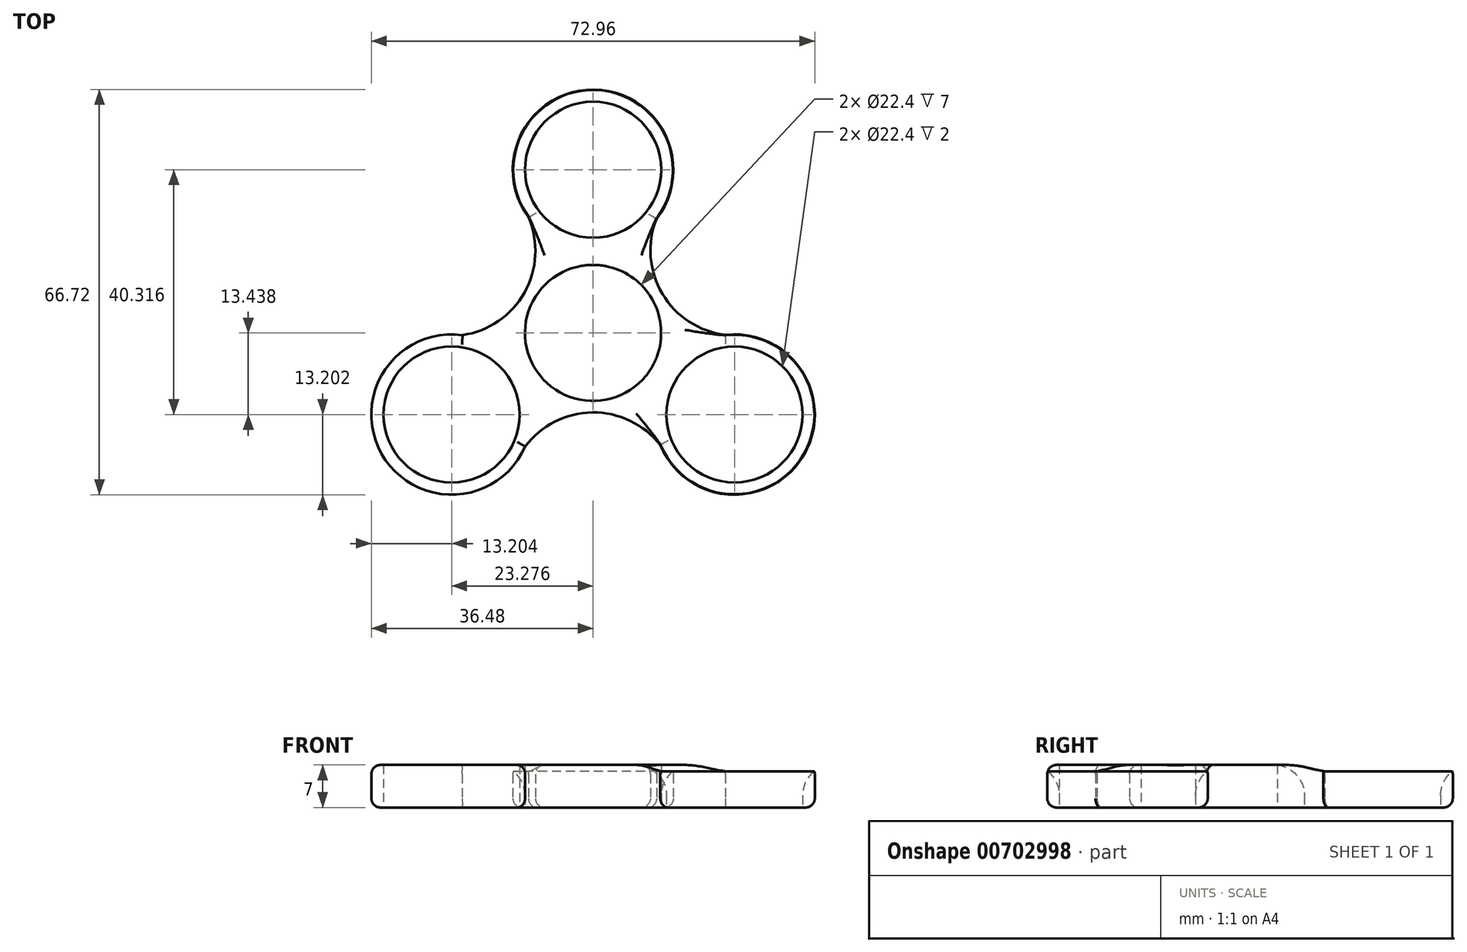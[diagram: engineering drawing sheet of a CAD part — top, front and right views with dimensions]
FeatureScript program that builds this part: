
annotation { "Feature Type Name" : "Feature", "Feature Type Description" : "" }
export const myFeature = defineFeature(function(context is Context, id is Id, definition is map)
    precondition{}
    {
        {
            var Q0;
            Q0=qCreatedBy(makeId("Top.planeOp"),FACE);
            var sketch = newSketch(context, id + "F0", { "sketchPlane" : qUnion([Q0])});
            skCircle(sketch, "E0", {"center": v(0, 0) * mm, "radius": 11.2 * mm});
            skCircle(sketch, "E1", {"center": v(0, 0) * mm, "radius": 13.2 * mm});
            skCircle(sketch, "E2", {"center": v(0, 26.88) * mm, "radius": 11.2 * mm});
            skArc(sketch, "E3", {"start": v(10.44, 18.8) * mm, "mid": v(0.14, 40.08) * mm, "end": v(-10.61, 19.03) * mm});
            skArc(sketch, "E4.1.0", {"start": v(-21.5, -0.36) * mm, "mid": v(-34.78, -19.92) * mm, "end": v(-11.17, -18.7) * mm});
            skCircle(sketch, "E4.1.1", {"center": v(-23.28, -13.44) * mm, "radius": 11.2 * mm});
            skArc(sketch, "E4.2.0", {"start": v(11.06, -18.44) * mm, "mid": v(34.64, -20.16) * mm, "end": v(21.78, -0.32) * mm});
            skCircle(sketch, "E4.2.1", {"center": v(23.28, -13.44) * mm, "radius": 11.2 * mm});
            skArc(sketch, "E5", {"start": v(10.44, 18.8) * mm, "mid": v(11.4, 6.44) * mm, "end": v(21.78, -0.32) * mm});
            skArc(sketch, "E6.1.0", {"start": v(-21.5, -0.36) * mm, "mid": v(-11.28, 6.65) * mm, "end": v(-10.61, 19.03) * mm});
            skArc(sketch, "E6.2.0", {"start": v(11.06, -18.44) * mm, "mid": v(-0.12, -13.1) * mm, "end": v(-11.17, -18.7) * mm});
            skSolve(sketch);
        }
        {
            var Q0;
            {var subQ1=sQuery(id+"F0.wireOp",EDGE,"E4.1.0");Q0=makeQuery(id+"F0.imprint","IMPRINT",FACE,{"disambiguationData":[TD([[makeQuery(id+"F0.imprint","IMPRINT",EDGE,{"derivedFrom":subQ1}),1.0]])]});}
            var Q1;
            Q1=makeQuery(id+"F0.imprint","IMPRINT",FACE,{"disambiguationData":[TD([[makeQuery(id+"F0.imprint","IMPRINT",EDGE,{"derivedFrom":sQuery(id+"F0.wireOp",EDGE,"E2")}),-1.0]])]});
            var Q2;
            Q2=makeQuery(id+"F0.imprint","IMPRINT",FACE,{"disambiguationData":[TD([[makeQuery(id+"F0.imprint","IMPRINT",EDGE,{"derivedFrom":sQuery(id+"F0.wireOp",EDGE,"E0")}),-1.0]])]});
            var Q3;
            {var subQ1=sQuery(id+"F0.wireOp",EDGE,"E4.2.0");Q3=makeQuery(id+"F0.imprint","IMPRINT",FACE,{"disambiguationData":[TD([[makeQuery(id+"F0.imprint","IMPRINT",EDGE,{"derivedFrom":subQ1}),1.0]])]});}
            extrude(context, id + "F1", {"entities" : qUnion([Q0, Q1, Q2, Q3]), "depth" : 7 * mm, "offsetDistance" : 25 * mm});
        }
        {
            var Q0;
            Q0=makeQuery(id+"F1.opExtrude","CAP_EDGE",EDGE,{"disambiguationData":[OSD([sQuery(id+"F0.wireOp",EDGE,"E4.1.0")])],"isStart":false});
            var Q1;
            Q1=makeQuery(id+"F1.opExtrude","CAP_EDGE",EDGE,{"disambiguationData":[OSD([sQuery(id+"F0.wireOp",EDGE,"E6.1.0")])],"isStart":false});
            var Q2;
            Q2=makeQuery(id+"F1.opExtrude","CAP_EDGE",EDGE,{"disambiguationData":[OSD([sQuery(id+"F0.wireOp",EDGE,"E6.2.0")])],"isStart":false});
            var Q3;
            Q3=makeQuery(id+"F1.opExtrude","CAP_EDGE",EDGE,{"disambiguationData":[OSD([sQuery(id+"F0.wireOp",EDGE,"E6.2.0")])],"isStart":true});
            var Q4;
            Q4=makeQuery(id+"F1.opExtrude","CAP_EDGE",EDGE,{"disambiguationData":[OSD([sQuery(id+"F0.wireOp",EDGE,"E3")])],"isStart":false});
            var Q5;
            Q5=makeQuery(id+"F1.opExtrude","CAP_EDGE",EDGE,{"disambiguationData":[OSD([sQuery(id+"F0.wireOp",EDGE,"E5")])],"isStart":false});
            var Q6;
            Q6=makeQuery(id+"F1.opExtrude","CAP_EDGE",EDGE,{"disambiguationData":[OSD([sQuery(id+"F0.wireOp",EDGE,"E4.2.0")])],"isStart":false});
            fillet(context, id + "F2", {"entities" : qUnion([Q0, Q1, Q2, Q3, Q4, Q5, Q6]), "radius" : 1.5 * mm, "tangentPropagation" : true, "allowEdgeOverflow" : false});
        }
        {
            var Q0;
            Q0=makeQuery(id+"F1.opExtrude","CAP_EDGE",EDGE,{"disambiguationData":[OSD([sQuery(id+"F0.wireOp",EDGE,"E4.1.0")])],"isStart":true});
            var Q1;
            Q1=makeQuery(id+"F1.opExtrude","CAP_EDGE",EDGE,{"disambiguationData":[OSD([sQuery(id+"F0.wireOp",EDGE,"E6.1.0")])],"isStart":true});
            var Q2;
            Q2=makeQuery(id+"F1.opExtrude","CAP_EDGE",EDGE,{"disambiguationData":[OSD([sQuery(id+"F0.wireOp",EDGE,"E3")])],"isStart":true});
            var Q3;
            Q3=makeQuery(id+"F1.opExtrude","CAP_EDGE",EDGE,{"disambiguationData":[OSD([sQuery(id+"F0.wireOp",EDGE,"E5")])],"isStart":true});
            var Q4;
            Q4=makeQuery(id+"F1.opExtrude","CAP_EDGE",EDGE,{"disambiguationData":[OSD([sQuery(id+"F0.wireOp",EDGE,"E4.2.0")])],"isStart":true});
            var Q5;
            {var subQ0=sQuery(id+"F0.wireOp",EDGE,"E6.2.0");Q5=makeQuery(id+"F2.opFillet","BLEND_EDGE",EDGE,{"blendedFrom":[makeQuery(id+"F1.opExtrude","CAP_EDGE",EDGE,{"disambiguationData":[OSD([subQ0])],"isStart":true}),makeQuery(id+"F1.opExtrude","CAP_FACE",FACE,{"disambiguationData":[OSD([sQuery(id+"F0.wireOp",EDGE,"E0"),sQuery(id+"F0.wireOp",EDGE,"E2"),sQuery(id+"F0.wireOp",EDGE,"E3"),sQuery(id+"F0.wireOp",EDGE,"E4.1.0"),sQuery(id+"F0.wireOp",EDGE,"E4.1.1"),sQuery(id+"F0.wireOp",EDGE,"E4.2.0"),sQuery(id+"F0.wireOp",EDGE,"E4.2.1"),sQuery(id+"F0.wireOp",EDGE,"E5"),sQuery(id+"F0.wireOp",EDGE,"E6.1.0"),subQ0])],"isStart":true})],"blendedInto":[makeQuery(id+"F1.opExtrude","CAP_FACE",FACE,{"disambiguationData":[OSD([sQuery(id+"F0.wireOp",EDGE,"E0"),sQuery(id+"F0.wireOp",EDGE,"E2"),sQuery(id+"F0.wireOp",EDGE,"E3"),sQuery(id+"F0.wireOp",EDGE,"E4.1.0"),sQuery(id+"F0.wireOp",EDGE,"E4.1.1"),sQuery(id+"F0.wireOp",EDGE,"E4.2.0"),sQuery(id+"F0.wireOp",EDGE,"E4.2.1"),sQuery(id+"F0.wireOp",EDGE,"E5"),sQuery(id+"F0.wireOp",EDGE,"E6.1.0"),subQ0])],"isStart":true})]});}
            fillet(context, id + "F3", {"entities" : qUnion([Q0, Q1, Q2, Q3, Q4, Q5]), "radius" : 1.5 * mm, "tangentPropagation" : true, "allowEdgeOverflow" : false});
        }
        {
            var Q0;
            {var subQ0=sQuery(id+"F0.wireOp",EDGE,"E6.2.0");Q0=makeQuery(id+"F2.opFillet","BLEND_EDGE",EDGE,{"blendedFrom":[makeQuery(id+"F1.opExtrude","CAP_EDGE",EDGE,{"disambiguationData":[OSD([subQ0])],"isStart":false}),makeQuery(id+"F1.opExtrude","CAP_FACE",FACE,{"disambiguationData":[OSD([sQuery(id+"F0.wireOp",EDGE,"E0"),sQuery(id+"F0.wireOp",EDGE,"E2"),sQuery(id+"F0.wireOp",EDGE,"E3"),sQuery(id+"F0.wireOp",EDGE,"E4.1.0"),sQuery(id+"F0.wireOp",EDGE,"E4.1.1"),sQuery(id+"F0.wireOp",EDGE,"E4.2.0"),sQuery(id+"F0.wireOp",EDGE,"E4.2.1"),sQuery(id+"F0.wireOp",EDGE,"E5"),sQuery(id+"F0.wireOp",EDGE,"E6.1.0"),subQ0])],"isStart":false})],"blendedInto":[makeQuery(id+"F1.opExtrude","CAP_FACE",FACE,{"disambiguationData":[OSD([sQuery(id+"F0.wireOp",EDGE,"E0"),sQuery(id+"F0.wireOp",EDGE,"E2"),sQuery(id+"F0.wireOp",EDGE,"E3"),sQuery(id+"F0.wireOp",EDGE,"E4.1.0"),sQuery(id+"F0.wireOp",EDGE,"E4.1.1"),sQuery(id+"F0.wireOp",EDGE,"E4.2.0"),sQuery(id+"F0.wireOp",EDGE,"E4.2.1"),sQuery(id+"F0.wireOp",EDGE,"E5"),sQuery(id+"F0.wireOp",EDGE,"E6.1.0"),subQ0])],"isStart":false})]});}
            var Q1;
            {var subQ0=sQuery(id+"F0.wireOp",EDGE,"E4.1.0");Q1=makeQuery(id+"F2.opFillet","BLEND_EDGE",EDGE,{"blendedFrom":[makeQuery(id+"F1.opExtrude","CAP_EDGE",EDGE,{"disambiguationData":[OSD([subQ0])],"isStart":false}),makeQuery(id+"F1.opExtrude","SWEPT_FACE",FACE,{"disambiguationData":[OSD([subQ0])]})],"blendedInto":[makeQuery(id+"F1.opExtrude","SWEPT_FACE",FACE,{"disambiguationData":[OSD([subQ0])]})]});}
            var Q2;
            {var subQ0=sQuery(id+"F0.wireOp",EDGE,"E6.1.0");Q2=makeQuery(id+"F2.opFillet","BLEND_EDGE",EDGE,{"blendedFrom":[makeQuery(id+"F1.opExtrude","CAP_EDGE",EDGE,{"disambiguationData":[OSD([subQ0])],"isStart":false}),makeQuery(id+"F1.opExtrude","CAP_FACE",FACE,{"disambiguationData":[OSD([sQuery(id+"F0.wireOp",EDGE,"E0"),sQuery(id+"F0.wireOp",EDGE,"E2"),sQuery(id+"F0.wireOp",EDGE,"E3"),sQuery(id+"F0.wireOp",EDGE,"E4.1.0"),sQuery(id+"F0.wireOp",EDGE,"E4.1.1"),sQuery(id+"F0.wireOp",EDGE,"E4.2.0"),sQuery(id+"F0.wireOp",EDGE,"E4.2.1"),sQuery(id+"F0.wireOp",EDGE,"E5"),subQ0,sQuery(id+"F0.wireOp",EDGE,"E6.2.0")])],"isStart":false})],"blendedInto":[makeQuery(id+"F1.opExtrude","CAP_FACE",FACE,{"disambiguationData":[OSD([sQuery(id+"F0.wireOp",EDGE,"E0"),sQuery(id+"F0.wireOp",EDGE,"E2"),sQuery(id+"F0.wireOp",EDGE,"E3"),sQuery(id+"F0.wireOp",EDGE,"E4.1.0"),sQuery(id+"F0.wireOp",EDGE,"E4.1.1"),sQuery(id+"F0.wireOp",EDGE,"E4.2.0"),sQuery(id+"F0.wireOp",EDGE,"E4.2.1"),sQuery(id+"F0.wireOp",EDGE,"E5"),subQ0,sQuery(id+"F0.wireOp",EDGE,"E6.2.0")])],"isStart":false})]});}
            var Q3;
            Q3=makeQuery(id+"F1.opExtrude","CAP_EDGE",EDGE,{"disambiguationData":[OSD([sQuery(id+"F0.wireOp",EDGE,"E2")])],"isStart":false});
            var Q4;
            {var subQ0=sQuery(id+"F0.wireOp",EDGE,"E5");Q4=makeQuery(id+"F2.opFillet","BLEND_EDGE",EDGE,{"blendedFrom":[makeQuery(id+"F1.opExtrude","CAP_EDGE",EDGE,{"disambiguationData":[OSD([subQ0])],"isStart":false}),makeQuery(id+"F1.opExtrude","SWEPT_FACE",FACE,{"disambiguationData":[OSD([subQ0])]})],"blendedInto":[makeQuery(id+"F1.opExtrude","SWEPT_FACE",FACE,{"disambiguationData":[OSD([subQ0])]})]});}
            var Q5;
            Q5=makeQuery(id+"F1.opExtrude","CAP_EDGE",EDGE,{"disambiguationData":[OSD([sQuery(id+"F0.wireOp",EDGE,"E4.2.1")])],"isStart":false});
            var Q6;
            {var subQ0=sQuery(id+"F0.wireOp",EDGE,"E6.2.0");Q6=makeQuery(id+"F2.opFillet","BLEND_EDGE",EDGE,{"blendedFrom":[makeQuery(id+"F1.opExtrude","CAP_EDGE",EDGE,{"disambiguationData":[OSD([subQ0])],"isStart":true}),makeQuery(id+"F1.opExtrude","SWEPT_FACE",FACE,{"disambiguationData":[OSD([subQ0])]})],"blendedInto":[makeQuery(id+"F1.opExtrude","SWEPT_FACE",FACE,{"disambiguationData":[OSD([subQ0])]})]});}
            var Q7;
            {var subQ0=sQuery(id+"F0.wireOp",EDGE,"E4.1.0");Q7=makeQuery(id+"F3.opFillet","BLEND_EDGE",EDGE,{"blendedFrom":[makeQuery(id+"F1.opExtrude","CAP_EDGE",EDGE,{"disambiguationData":[OSD([subQ0])],"isStart":true}),makeQuery(id+"F1.opExtrude","SWEPT_FACE",FACE,{"disambiguationData":[OSD([subQ0])]})],"blendedInto":[makeQuery(id+"F1.opExtrude","SWEPT_FACE",FACE,{"disambiguationData":[OSD([subQ0])]})]});}
            var Q8;
            {var subQ0=sQuery(id+"F0.wireOp",EDGE,"E6.1.0");Q8=makeQuery(id+"F3.opFillet","BLEND_EDGE",EDGE,{"blendedFrom":[makeQuery(id+"F1.opExtrude","CAP_EDGE",EDGE,{"disambiguationData":[OSD([subQ0])],"isStart":true}),makeQuery(id+"F1.opExtrude","CAP_FACE",FACE,{"disambiguationData":[OSD([sQuery(id+"F0.wireOp",EDGE,"E0"),sQuery(id+"F0.wireOp",EDGE,"E2"),sQuery(id+"F0.wireOp",EDGE,"E3"),sQuery(id+"F0.wireOp",EDGE,"E4.1.0"),sQuery(id+"F0.wireOp",EDGE,"E4.1.1"),sQuery(id+"F0.wireOp",EDGE,"E4.2.0"),sQuery(id+"F0.wireOp",EDGE,"E4.2.1"),sQuery(id+"F0.wireOp",EDGE,"E5"),subQ0,sQuery(id+"F0.wireOp",EDGE,"E6.2.0")])],"isStart":true})],"blendedInto":[makeQuery(id+"F1.opExtrude","CAP_FACE",FACE,{"disambiguationData":[OSD([sQuery(id+"F0.wireOp",EDGE,"E0"),sQuery(id+"F0.wireOp",EDGE,"E2"),sQuery(id+"F0.wireOp",EDGE,"E3"),sQuery(id+"F0.wireOp",EDGE,"E4.1.0"),sQuery(id+"F0.wireOp",EDGE,"E4.1.1"),sQuery(id+"F0.wireOp",EDGE,"E4.2.0"),sQuery(id+"F0.wireOp",EDGE,"E4.2.1"),sQuery(id+"F0.wireOp",EDGE,"E5"),subQ0,sQuery(id+"F0.wireOp",EDGE,"E6.2.0")])],"isStart":true})]});}
            var Q9;
            {var subQ0=sQuery(id+"F0.wireOp",EDGE,"E3");Q9=makeQuery(id+"F3.opFillet","BLEND_EDGE",EDGE,{"blendedFrom":[makeQuery(id+"F1.opExtrude","CAP_EDGE",EDGE,{"disambiguationData":[OSD([subQ0])],"isStart":true}),makeQuery(id+"F1.opExtrude","CAP_FACE",FACE,{"disambiguationData":[OSD([sQuery(id+"F0.wireOp",EDGE,"E0"),sQuery(id+"F0.wireOp",EDGE,"E2"),subQ0,sQuery(id+"F0.wireOp",EDGE,"E4.1.0"),sQuery(id+"F0.wireOp",EDGE,"E4.1.1"),sQuery(id+"F0.wireOp",EDGE,"E4.2.0"),sQuery(id+"F0.wireOp",EDGE,"E4.2.1"),sQuery(id+"F0.wireOp",EDGE,"E5"),sQuery(id+"F0.wireOp",EDGE,"E6.1.0"),sQuery(id+"F0.wireOp",EDGE,"E6.2.0")])],"isStart":true})],"blendedInto":[makeQuery(id+"F1.opExtrude","CAP_FACE",FACE,{"disambiguationData":[OSD([sQuery(id+"F0.wireOp",EDGE,"E0"),sQuery(id+"F0.wireOp",EDGE,"E2"),subQ0,sQuery(id+"F0.wireOp",EDGE,"E4.1.0"),sQuery(id+"F0.wireOp",EDGE,"E4.1.1"),sQuery(id+"F0.wireOp",EDGE,"E4.2.0"),sQuery(id+"F0.wireOp",EDGE,"E4.2.1"),sQuery(id+"F0.wireOp",EDGE,"E5"),sQuery(id+"F0.wireOp",EDGE,"E6.1.0"),sQuery(id+"F0.wireOp",EDGE,"E6.2.0")])],"isStart":true})]});}
            var Q10;
            {var subQ0=sQuery(id+"F0.wireOp",EDGE,"E5");Q10=makeQuery(id+"F3.opFillet","BLEND_EDGE",EDGE,{"blendedFrom":[makeQuery(id+"F1.opExtrude","CAP_EDGE",EDGE,{"disambiguationData":[OSD([subQ0])],"isStart":true}),makeQuery(id+"F1.opExtrude","CAP_FACE",FACE,{"disambiguationData":[OSD([sQuery(id+"F0.wireOp",EDGE,"E0"),sQuery(id+"F0.wireOp",EDGE,"E2"),sQuery(id+"F0.wireOp",EDGE,"E3"),sQuery(id+"F0.wireOp",EDGE,"E4.1.0"),sQuery(id+"F0.wireOp",EDGE,"E4.1.1"),sQuery(id+"F0.wireOp",EDGE,"E4.2.0"),sQuery(id+"F0.wireOp",EDGE,"E4.2.1"),subQ0,sQuery(id+"F0.wireOp",EDGE,"E6.1.0"),sQuery(id+"F0.wireOp",EDGE,"E6.2.0")])],"isStart":true})],"blendedInto":[makeQuery(id+"F1.opExtrude","CAP_FACE",FACE,{"disambiguationData":[OSD([sQuery(id+"F0.wireOp",EDGE,"E0"),sQuery(id+"F0.wireOp",EDGE,"E2"),sQuery(id+"F0.wireOp",EDGE,"E3"),sQuery(id+"F0.wireOp",EDGE,"E4.1.0"),sQuery(id+"F0.wireOp",EDGE,"E4.1.1"),sQuery(id+"F0.wireOp",EDGE,"E4.2.0"),sQuery(id+"F0.wireOp",EDGE,"E4.2.1"),subQ0,sQuery(id+"F0.wireOp",EDGE,"E6.1.0"),sQuery(id+"F0.wireOp",EDGE,"E6.2.0")])],"isStart":true})]});}
            var Q11;
            {var subQ0=sQuery(id+"F0.wireOp",EDGE,"E4.2.0");Q11=makeQuery(id+"F3.opFillet","BLEND_EDGE",EDGE,{"blendedFrom":[makeQuery(id+"F1.opExtrude","CAP_EDGE",EDGE,{"disambiguationData":[OSD([subQ0])],"isStart":true}),makeQuery(id+"F1.opExtrude","CAP_FACE",FACE,{"disambiguationData":[OSD([sQuery(id+"F0.wireOp",EDGE,"E0"),sQuery(id+"F0.wireOp",EDGE,"E2"),sQuery(id+"F0.wireOp",EDGE,"E3"),sQuery(id+"F0.wireOp",EDGE,"E4.1.0"),sQuery(id+"F0.wireOp",EDGE,"E4.1.1"),subQ0,sQuery(id+"F0.wireOp",EDGE,"E4.2.1"),sQuery(id+"F0.wireOp",EDGE,"E5"),sQuery(id+"F0.wireOp",EDGE,"E6.1.0"),sQuery(id+"F0.wireOp",EDGE,"E6.2.0")])],"isStart":true})],"blendedInto":[makeQuery(id+"F1.opExtrude","CAP_FACE",FACE,{"disambiguationData":[OSD([sQuery(id+"F0.wireOp",EDGE,"E0"),sQuery(id+"F0.wireOp",EDGE,"E2"),sQuery(id+"F0.wireOp",EDGE,"E3"),sQuery(id+"F0.wireOp",EDGE,"E4.1.0"),sQuery(id+"F0.wireOp",EDGE,"E4.1.1"),subQ0,sQuery(id+"F0.wireOp",EDGE,"E4.2.1"),sQuery(id+"F0.wireOp",EDGE,"E5"),sQuery(id+"F0.wireOp",EDGE,"E6.1.0"),sQuery(id+"F0.wireOp",EDGE,"E6.2.0")])],"isStart":true})]});}
            fillet(context, id + "F4", {"entities" : qUnion([Q0, Q1, Q2, Q3, Q4, Q5, Q6, Q7, Q8, Q9, Q10, Q11]), "radius" : 5 * mm, "tangentPropagation" : true, "allowEdgeOverflow" : false});
        }
    });
